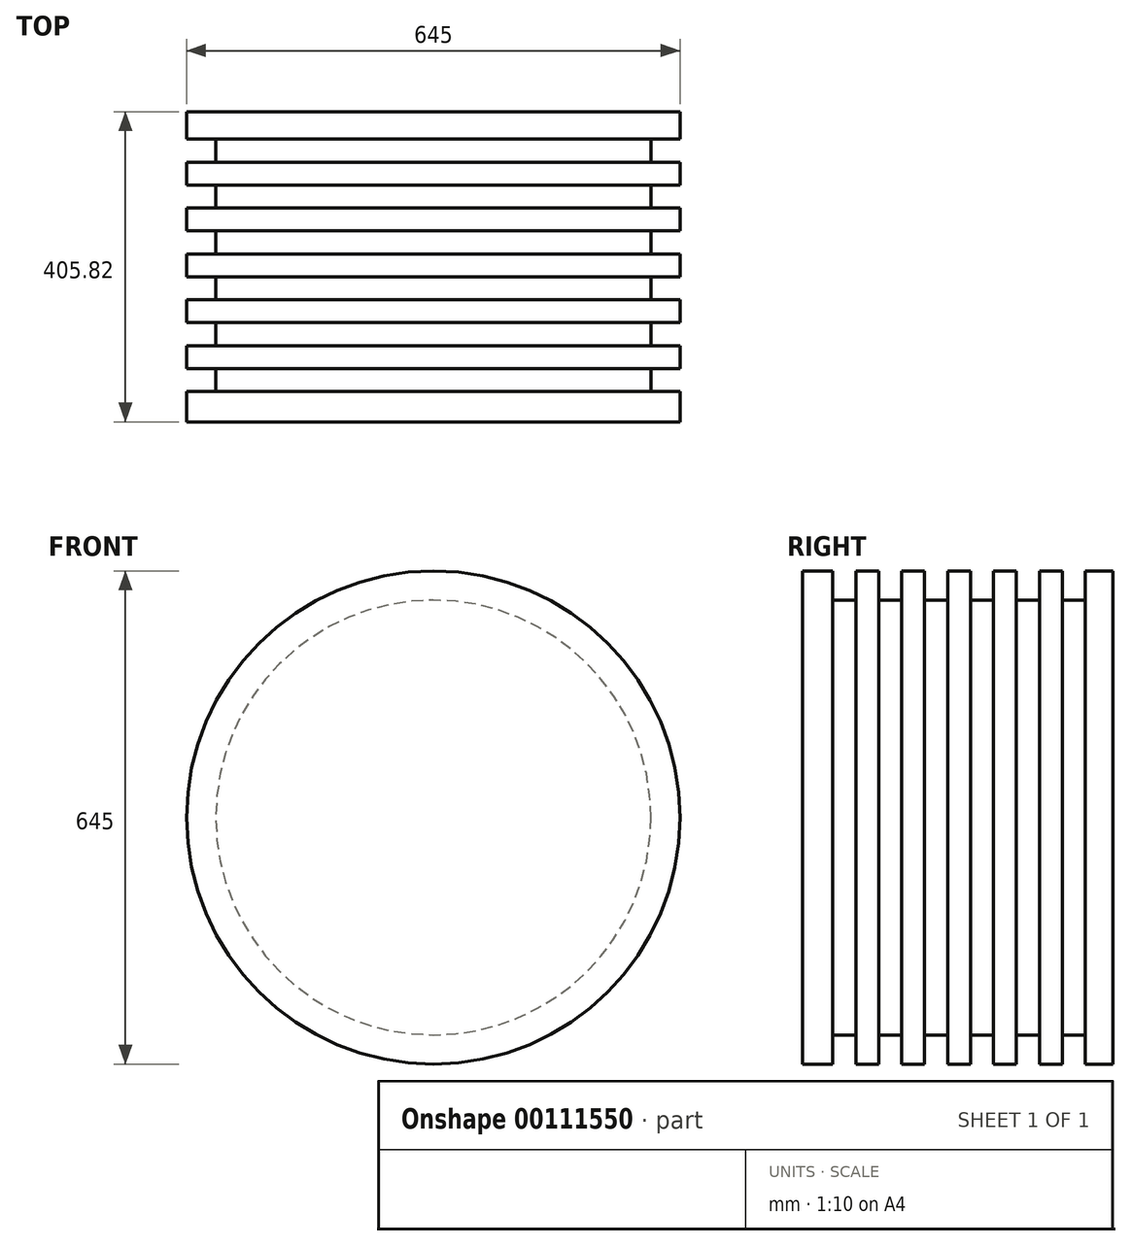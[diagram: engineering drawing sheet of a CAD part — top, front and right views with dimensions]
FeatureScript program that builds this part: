
annotation { "Feature Type Name" : "Feature", "Feature Type Description" : "" }
export const myFeature = defineFeature(function(context is Context, id is Id, definition is map)
    precondition{}
    {
        {
            var Q0;
            Q0=qCreatedBy(makeId("Front.planeOp"),FACE);
            var sketch = newSketch(context, id + "F0", { "sketchPlane" : qUnion([Q0])});
            skCircle(sketch, "E0", {"center": v(0, 0) * mm, "radius": 322.5 * mm});
            skSolve(sketch);
        }
        {
            var Q0;
            Q0 = qSketchRegion(id + "F0", true);
            extrude(context, id + "F1", {"entities" : qUnion([Q0]), "depth" : 405.82 * mm});
        }
        {
            var Q0;
            Q0=qCreatedBy(makeId("Right.planeOp"),FACE);
            var sketch = newSketch(context, id + "F2", { "sketchPlane" : qUnion([Q0])});
            skLineSegment(sketch, "E1.bottom", {"start": v(-366.07, 340.51) * mm, "end": v(-336.07, 340.51) * mm});
            skLineSegment(sketch, "E1.top", {"start": v(-366.07, 284.36) * mm, "end": v(-336.07, 284.36) * mm});
            skLineSegment(sketch, "E1.left", {"start": v(-366.07, 340.51) * mm, "end": v(-366.07, 284.36) * mm});
            skLineSegment(sketch, "E1.right", {"start": v(-336.07, 340.51) * mm, "end": v(-336.07, 284.36) * mm});
            skLineSegment(sketch, "E2.1.0.0", {"start": v(-276.07, 340.51) * mm, "end": v(-276.07, 284.36) * mm});
            skLineSegment(sketch, "E2.1.0.1", {"start": v(-306.07, 340.51) * mm, "end": v(-306.07, 284.36) * mm});
            skLineSegment(sketch, "E2.1.0.2", {"start": v(-306.07, 284.36) * mm, "end": v(-276.07, 284.36) * mm});
            skLineSegment(sketch, "E2.1.0.3", {"start": v(-306.07, 340.51) * mm, "end": v(-276.07, 340.51) * mm});
            skLineSegment(sketch, "E2.2.0.0", {"start": v(-216.07, 340.51) * mm, "end": v(-216.07, 284.36) * mm});
            skLineSegment(sketch, "E2.2.0.1", {"start": v(-246.07, 340.51) * mm, "end": v(-246.07, 284.36) * mm});
            skLineSegment(sketch, "E2.2.0.2", {"start": v(-246.07, 284.36) * mm, "end": v(-216.07, 284.36) * mm});
            skLineSegment(sketch, "E2.2.0.3", {"start": v(-246.07, 340.51) * mm, "end": v(-216.07, 340.51) * mm});
            skLineSegment(sketch, "E2.3.0.0", {"start": v(-156.07, 340.51) * mm, "end": v(-156.07, 284.36) * mm});
            skLineSegment(sketch, "E2.3.0.1", {"start": v(-186.07, 340.51) * mm, "end": v(-186.07, 284.36) * mm});
            skLineSegment(sketch, "E2.3.0.2", {"start": v(-186.07, 284.36) * mm, "end": v(-156.07, 284.36) * mm});
            skLineSegment(sketch, "E2.3.0.3", {"start": v(-186.07, 340.51) * mm, "end": v(-156.07, 340.51) * mm});
            skLineSegment(sketch, "E2.4.0.0", {"start": v(-96.07, 340.51) * mm, "end": v(-96.07, 284.36) * mm});
            skLineSegment(sketch, "E2.4.0.1", {"start": v(-126.07, 340.51) * mm, "end": v(-126.07, 284.36) * mm});
            skLineSegment(sketch, "E2.4.0.2", {"start": v(-126.07, 284.36) * mm, "end": v(-96.07, 284.36) * mm});
            skLineSegment(sketch, "E2.4.0.3", {"start": v(-126.07, 340.51) * mm, "end": v(-96.07, 340.51) * mm});
            skLineSegment(sketch, "E2.5.0.0", {"start": v(-36.07, 340.51) * mm, "end": v(-36.07, 284.36) * mm});
            skLineSegment(sketch, "E2.5.0.1", {"start": v(-66.07, 340.51) * mm, "end": v(-66.07, 284.36) * mm});
            skLineSegment(sketch, "E2.5.0.2", {"start": v(-66.07, 284.36) * mm, "end": v(-36.07, 284.36) * mm});
            skLineSegment(sketch, "E2.5.0.3", {"start": v(-66.07, 340.51) * mm, "end": v(-36.07, 340.51) * mm});
            skLineSegment(sketch, "E2.direction1", {"start": v(-366.07, 284.36) * mm, "end": v(-306.07, 284.36) * mm, "construction": true});
            skLineSegment(sketch, "E3", {"start": v(0, 0) * mm, "end": v(-482.61, 0) * mm, "construction": true});
            skSolve(sketch);
        }
        {
            var Q0;
            Q0=makeQuery(id+"F2.imprint","IMPRINT",FACE,{"disambiguationData":[TD([[makeQuery(id+"F2.imprint","IMPRINT",EDGE,{"derivedFrom":sQuery(id+"F2.wireOp",EDGE,"E1.bottom")}),-1.0]])]});
            var Q1;
            Q1=makeQuery(id+"F2.imprint","IMPRINT",FACE,{"disambiguationData":[TD([[makeQuery(id+"F2.imprint","IMPRINT",EDGE,{"derivedFrom":sQuery(id+"F2.wireOp",EDGE,"E2.1.0.0")}),-1.0]])]});
            var Q2;
            Q2=makeQuery(id+"F2.imprint","IMPRINT",FACE,{"disambiguationData":[TD([[makeQuery(id+"F2.imprint","IMPRINT",EDGE,{"derivedFrom":sQuery(id+"F2.wireOp",EDGE,"E2.2.0.0")}),-1.0]])]});
            var Q3;
            Q3=makeQuery(id+"F2.imprint","IMPRINT",FACE,{"disambiguationData":[TD([[makeQuery(id+"F2.imprint","IMPRINT",EDGE,{"derivedFrom":sQuery(id+"F2.wireOp",EDGE,"E2.3.0.0")}),-1.0]])]});
            var Q4;
            Q4=makeQuery(id+"F2.imprint","IMPRINT",FACE,{"disambiguationData":[TD([[makeQuery(id+"F2.imprint","IMPRINT",EDGE,{"derivedFrom":sQuery(id+"F2.wireOp",EDGE,"E2.4.0.0")}),-1.0]])]});
            var Q5;
            Q5=makeQuery(id+"F2.imprint","IMPRINT",FACE,{"disambiguationData":[TD([[makeQuery(id+"F2.imprint","IMPRINT",EDGE,{"derivedFrom":sQuery(id+"F2.wireOp",EDGE,"E2.5.0.0")}),-1.0]])]});
            var Q6;
            Q6=sQuery(id+"F2.wireOp",EDGE,"E2.1.0.3");
            var Q7;
            Q7=sQuery(id+"F2.wireOp",EDGE,"E2.2.0.0");
            var Q8;
            Q8=sQuery(id+"F2.wireOp",EDGE,"E2.2.0.1");
            var Q9;
            Q9=sQuery(id+"F2.wireOp",EDGE,"E2.2.0.2");
            var Q10;
            Q10=sQuery(id+"F2.wireOp",EDGE,"E2.2.0.3");
            var Q11;
            Q11=sQuery(id+"F2.wireOp",EDGE,"E2.3.0.0");
            var Q12;
            Q12=sQuery(id+"F2.wireOp",EDGE,"E2.5.0.3");
            var Q13;
            Q13=sQuery(id+"F2.wireOp",EDGE,"E2.5.0.2");
            var Q14;
            Q14=sQuery(id+"F2.wireOp",EDGE,"E2.5.0.0");
            var Q15;
            Q15=sQuery(id+"F2.wireOp",EDGE,"E2.4.0.2");
            var Q16;
            Q16=sQuery(id+"F2.wireOp",EDGE,"E2.4.0.0");
            var Q17;
            Q17=sQuery(id+"F2.wireOp",EDGE,"E2.5.0.1");
            var Q18;
            Q18=sQuery(id+"F2.wireOp",EDGE,"E2.4.0.3");
            var Q19;
            Q19=sQuery(id+"F2.wireOp",EDGE,"E2.4.0.1");
            var Q20;
            Q20=sQuery(id+"F2.wireOp",EDGE,"E2.3.0.1");
            var Q21;
            Q21=sQuery(id+"F2.wireOp",EDGE,"E2.3.0.2");
            var Q22;
            Q22=sQuery(id+"F2.wireOp",EDGE,"E2.3.0.3");
            var Q23;
            Q23=sQuery(id+"F2.wireOp",EDGE,"E1.bottom");
            var Q24;
            Q24=sQuery(id+"F2.wireOp",EDGE,"E1.left");
            var Q25;
            Q25=sQuery(id+"F2.wireOp",EDGE,"E1.right");
            var Q26;
            Q26=sQuery(id+"F2.wireOp",EDGE,"E2.1.0.0");
            var Q27;
            Q27=sQuery(id+"F2.wireOp",EDGE,"E2.1.0.1");
            var Q28;
            Q28=sQuery(id+"F2.wireOp",EDGE,"E2.1.0.2");
            var Q29;
            Q29=sQuery(id+"F2.wireOp",EDGE,"E1.top");
            var Q30;
            Q30=sQuery(id+"F2.wireOp",EDGE,"E3");
            revolve(context, id + "F3", {"operationType" : NewBodyOperationType.REMOVE, "entities" : qUnion([Q0, Q1, Q2, Q3, Q4, Q5]), "surfaceEntities" : qUnion([Q6, Q7, Q8, Q9, Q10, Q11, Q12, Q13, Q14, Q15, Q16, Q17, Q18, Q19, Q20, Q21, Q22, Q23, Q24, Q25, Q26, Q27, Q28, Q29]), "axis" : qUnion([Q30]), "revolveType" : RevolveType.FULL, "oppositeDirection" : true});
        }
    });
